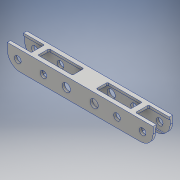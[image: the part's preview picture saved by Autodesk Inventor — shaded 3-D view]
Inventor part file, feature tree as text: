
AUTODESK INVENTOR PART (.ipt)
format: ipt  version: 2017 (Build 210142000, 142)  size: 280,576 bytes
history: native  units: mm
features: extrude x4, sketch x4, fillet x1
ambient origin geometry x8: Origin, YZ Plane, XZ Plane, XY Plane, X Axis, Y Axis, Z Axis, Center Point
bodies: Solid1 (feature_tree)
feature tree (9):
  extrude  "Extrusion1"  Depth=9.525mm TaperAngle=0.0deg
  extrude  "Extrusion2"  Depth=9.525mm TaperAngle=0.0deg
  extrude  "Extrusion3"  Depth=9.525mm TaperAngle=0.0deg
  extrude  "Extrusion5"  Depth=9.525mm TaperAngle=0.0deg
  fillet  "Fillet1"  Radius=50.0mm
  sketch  "Sketch1"  dims[d0=135.4mm d1=44.0mm d2=78.105mm d3=50.8mm d4=44.45mm d5=21.59mm d6=135.4mm d7=44.0mm d8=78.105mm d9=50.8mm d10=568.96mm d11=21.59mm d12=9.525mm d13=0.0mm]
  sketch  "Sketch2"  dims[d14=26.0mm d15=26.0mm d16=32.0mm d17=26.0mm d18=26.0mm d19=32.0mm d20=568.96mm d21=57.15mm d22=40.64mm d23=140.776mm d24=230.152mm d25=230.152mm d26=40.64mm d27=140.776mm d28=9.525mm d29=0.0mm]
  sketch  "Sketch3"  dims[d30=26.0mm d31=26.0mm d32=32.0mm d33=26.0mm d34=26.0mm d35=32.0mm d36=568.96mm d37=57.15mm d38=40.64mm d39=140.776mm d40=230.152mm d41=230.152mm d42=40.64mm d43=140.776mm d44=9.525mm d45=0.0mm]
  sketch  "Sketch5"  dims[d60=135.4mm d61=44.0mm d62=78.105mm d63=50.8mm d64=44.45mm d65=21.59mm d66=135.4mm d67=44.0mm d68=78.105mm d69=50.8mm d70=568.96mm d71=21.59mm d72=9.525mm d73=0.0mm d74=50.0mm]
